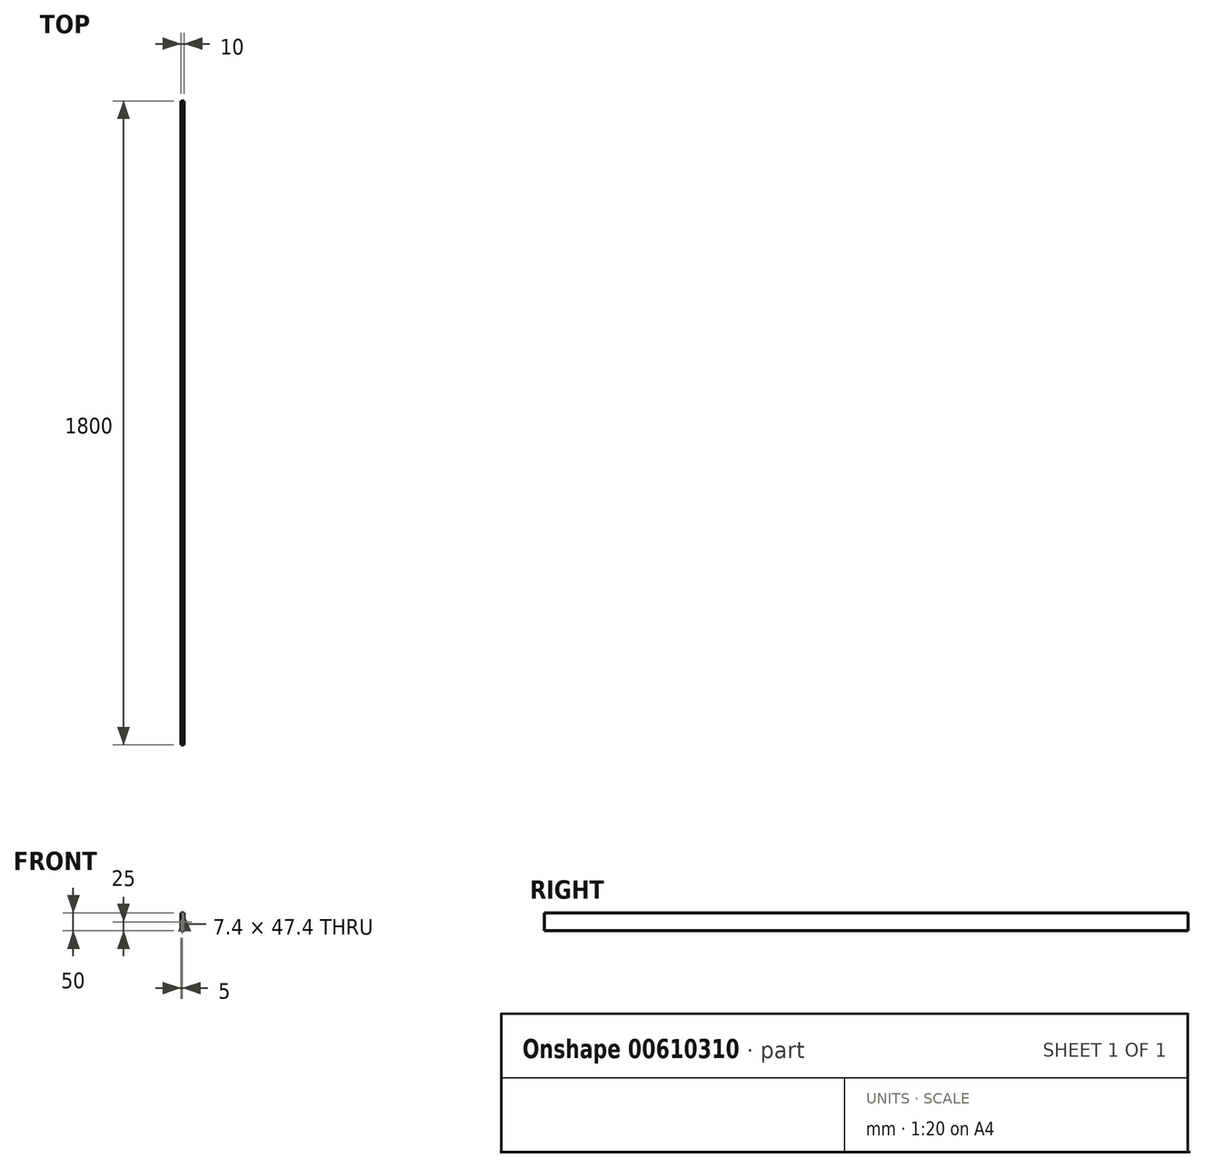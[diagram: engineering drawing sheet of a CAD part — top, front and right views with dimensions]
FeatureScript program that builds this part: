
annotation { "Feature Type Name" : "Feature", "Feature Type Description" : "" }
export const myFeature = defineFeature(function(context is Context, id is Id, definition is map)
    precondition{}
    {
        {
            var Q0;
            Q0=qCreatedBy(makeId("Front.planeOp"),FACE);
            var sketch = newSketch(context, id + "F0", { "sketchPlane" : qUnion([Q0])});
            skLineSegment(sketch, "E0.bottom", {"start": v(-5, 25) * mm, "end": v(5, 25) * mm});
            skLineSegment(sketch, "E0.top", {"start": v(-5, -25) * mm, "end": v(5, -25) * mm});
            skLineSegment(sketch, "E0.left", {"start": v(-5, 25) * mm, "end": v(-5, -25) * mm});
            skLineSegment(sketch, "E0.right", {"start": v(5, 25) * mm, "end": v(5, -25) * mm});
            skLineSegment(sketch, "E1", {"start": v(0, 0) * mm, "end": v(-5, 0) * mm, "construction": true});
            skLineSegment(sketch, "E2.bottom", {"start": v(-3.7, 23.7) * mm, "end": v(3.7, 23.7) * mm});
            skLineSegment(sketch, "E2.top", {"start": v(-3.7, -23.7) * mm, "end": v(3.7, -23.7) * mm});
            skLineSegment(sketch, "E2.left", {"start": v(-3.7, 23.7) * mm, "end": v(-3.7, -23.7) * mm});
            skLineSegment(sketch, "E2.right", {"start": v(3.7, 23.7) * mm, "end": v(3.7, -23.7) * mm});
            skLineSegment(sketch, "E3", {"start": v(0, 0) * mm, "end": v(0, 25) * mm, "construction": true});
            skLineSegment(sketch, "E4", {"start": v(-3.7, 2.74) * mm, "end": v(-5, 2.74) * mm, "construction": true});
            skLineSegment(sketch, "E5", {"start": v(3.7, 2.56) * mm, "end": v(5, 2.56) * mm, "construction": true});
            skLineSegment(sketch, "E6", {"start": v(0, -23.7) * mm, "end": v(0, -25) * mm, "construction": true});
            skLineSegment(sketch, "E7", {"start": v(-1.26, 23.7) * mm, "end": v(-1.26, 25) * mm, "construction": true});
            skLineSegment(sketch, "E8", {"start": v(0, 0) * mm, "end": v(5, 0) * mm, "construction": true});
            skLineSegment(sketch, "E9", {"start": v(0, 0) * mm, "end": v(0, -25) * mm, "construction": true});
            skLineSegment(sketch, "E10", {"start": v(0, 0) * mm, "end": v(-17.74, 0) * mm, "construction": true});
            skLineSegment(sketch, "E11", {"start": v(0, 0) * mm, "end": v(0, -41.92) * mm, "construction": true});
            skLineSegment(sketch, "E12", {"start": v(0, 0) * mm, "end": v(0, 40) * mm, "construction": true});
            skLineSegment(sketch, "E13", {"start": v(0, 0) * mm, "end": v(19.45, 0) * mm, "construction": true});
            skSolve(sketch);
        }
        {
            var Q0;
            Q0=makeQuery(id+"F0.imprint","IMPRINT",FACE,{"disambiguationData":[TD([[makeQuery(id+"F0.imprint","IMPRINT",EDGE,{"derivedFrom":sQuery(id+"F0.wireOp",EDGE,"E0.bottom")}),-1.0]])]});
            extrude(context, id + "F1", {"entities" : qUnion([Q0]), "depth" : 1800 * mm, "offsetDistance" : 25 * mm});
        }
    });
